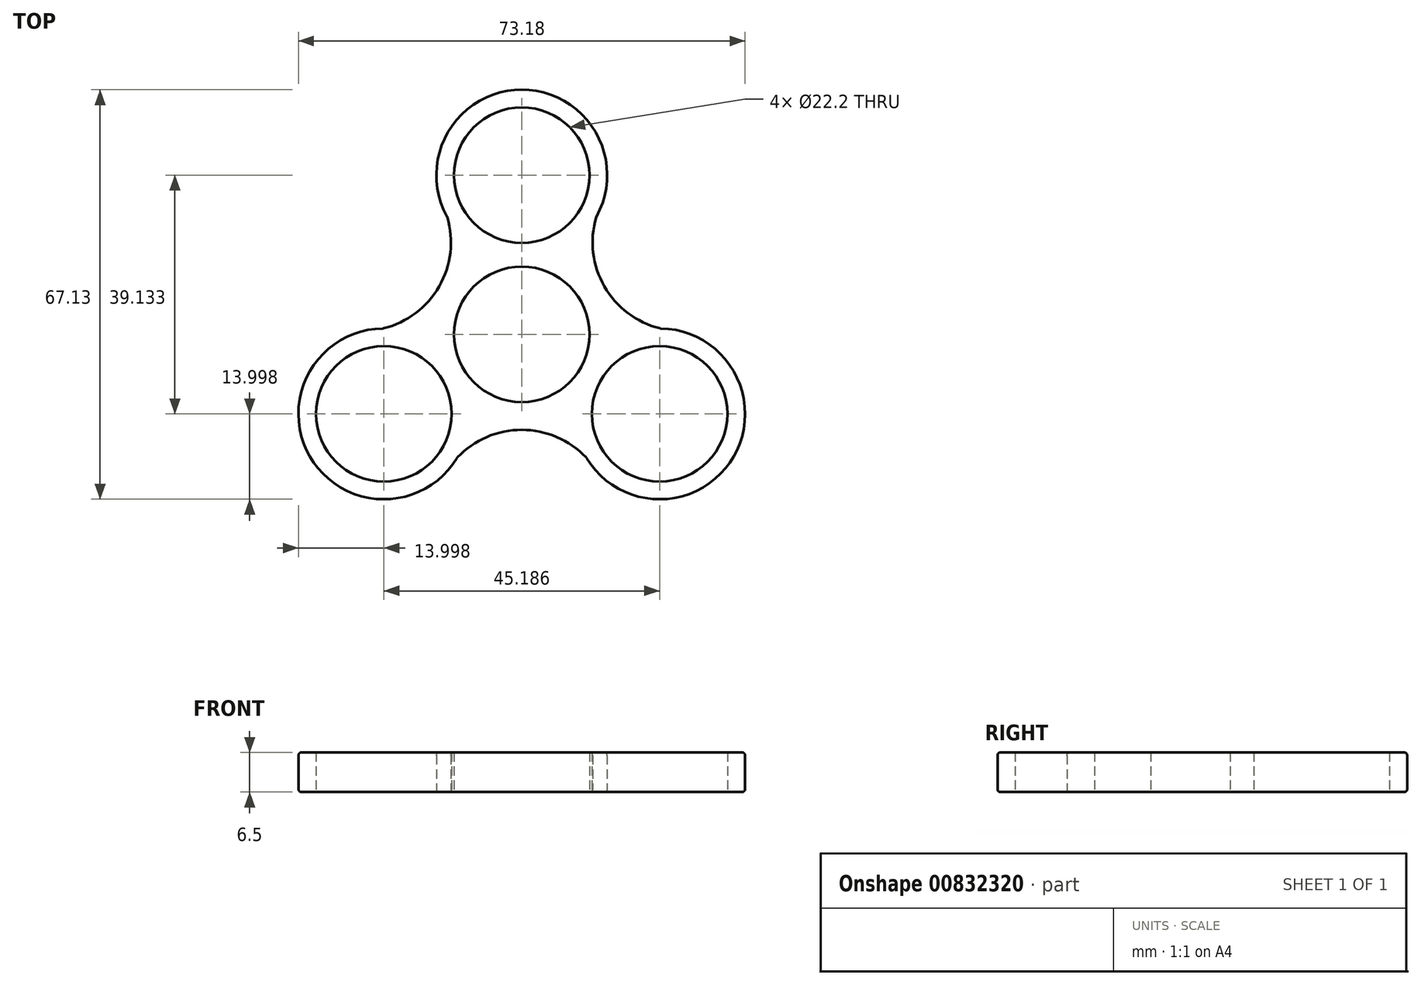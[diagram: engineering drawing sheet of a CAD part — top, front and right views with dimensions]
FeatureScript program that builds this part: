
annotation { "Feature Type Name" : "Feature", "Feature Type Description" : "" }
export const myFeature = defineFeature(function(context is Context, id is Id, definition is map)
    precondition{}
    {
        {
            var Q0;
            Q0=qCreatedBy(makeId("Top.planeOp"),FACE);
            var sketch = newSketch(context, id + "F0", { "sketchPlane" : qUnion([Q0])});
            skCircle(sketch, "E0", {"center": v(0, 0) * mm, "radius": 11.1 * mm});
            skCircle(sketch, "E1", {"center": v(0, 0) * mm, "radius": 14 * mm});
            skCircle(sketch, "E2", {"center": v(0, 26.1) * mm, "radius": 14 * mm});
            skCircle(sketch, "E3", {"center": v(0, 26.1) * mm, "radius": 11.1 * mm});
            skCircle(sketch, "E4.1.0", {"center": v(-22.6, -13.03) * mm, "radius": 11.1 * mm});
            skCircle(sketch, "E4.1.1", {"center": v(-22.6, -13.03) * mm, "radius": 14 * mm});
            skCircle(sketch, "E4.2.0", {"center": v(22.6, -13.03) * mm, "radius": 11.1 * mm});
            skCircle(sketch, "E4.2.1", {"center": v(22.6, -13.03) * mm, "radius": 14 * mm});
            skPoint(sketch, "E4.center", {"position": v(0, 0.01) * mm});
            skArc(sketch, "E5", {"start": v(12.47, -22.7) * mm, "mid": v(0, -15.65) * mm, "end": v(-12.47, -22.7) * mm});
            skArc(sketch, "E6.1.0", {"start": v(13.43, 22.15) * mm, "mid": v(13.55, 7.83) * mm, "end": v(25.9, 0.55) * mm});
            skArc(sketch, "E6.2.0", {"start": v(-25.9, 0.55) * mm, "mid": v(-13.56, 7.82) * mm, "end": v(-13.43, 22.15) * mm});
            skSolve(sketch);
        }
        {
            var Q0;
            Q0 = qSketchRegion(id + "F0", true);
            var Q1;
            Q1=makeQuery(id+"F0.imprint","IMPRINT",FACE,{"disambiguationData":[TD([[makeQuery(id+"F0.imprint","IMPRINT",EDGE,{"derivedFrom":sQuery(id+"F0.wireOp",EDGE,"E0")}),-1.0]])]});
            var Q2;
            {var subQ0=sQuery(id+"F0.wireOp",EDGE,"E4.1.1");var subQ1=sQuery(id+"F0.wireOp",EDGE,"E1");var subQ2=makeQuery(id+"F0.imprint","INTERSECT",VERTEX,{"disambiguationData":[OD(0.0)],"derivedFrom":[subQ1,subQ0]});Q2=makeQuery(id+"F0.imprint","IMPRINT",FACE,{"disambiguationData":[TD([[makeQuery(id+"F0.imprint","IMPRINT",EDGE,{"disambiguationData":[TD([[subQ2,-1.0]])],"derivedFrom":subQ1}),1.0]])]});}
            var Q3;
            {var subQ0=sQuery(id+"F0.wireOp",EDGE,"E4.2.1");var subQ1=sQuery(id+"F0.wireOp",EDGE,"E1");var subQ2=makeQuery(id+"F0.imprint","INTERSECT",VERTEX,{"disambiguationData":[OD(0.0)],"derivedFrom":[subQ1,subQ0]});Q3=makeQuery(id+"F0.imprint","IMPRINT",FACE,{"disambiguationData":[TD([[makeQuery(id+"F0.imprint","IMPRINT",EDGE,{"disambiguationData":[TD([[subQ2,-1.0]])],"derivedFrom":subQ1}),1.0]])]});}
            var Q4;
            {var subQ0=sQuery(id+"F0.wireOp",EDGE,"E2");var subQ1=sQuery(id+"F0.wireOp",EDGE,"E1");var subQ2=makeQuery(id+"F0.imprint","INTERSECT",VERTEX,{"disambiguationData":[OD(0.0)],"derivedFrom":[subQ1,subQ0]});Q4=makeQuery(id+"F0.imprint","IMPRINT",FACE,{"disambiguationData":[TD([[makeQuery(id+"F0.imprint","IMPRINT",EDGE,{"disambiguationData":[TD([[subQ2,1.0]])],"derivedFrom":subQ1}),1.0]])]});}
            extrude(context, id + "F1", {"entities" : qUnion([Q0, Q1, Q2, Q3, Q4]), "depth" : 6.5 * mm, "offsetDistance" : 25 * mm});
        }
        {
            var Q0;
            Q0=makeQuery(id+"F1.opExtrude","SWEPT_FACE",FACE,{"disambiguationData":[OSD([sQuery(id+"F0.wireOp",EDGE,"E4.1.1")])]});
            var Q1;
            Q1=makeQuery(id+"F1.opExtrude","SWEPT_FACE",FACE,{"disambiguationData":[OSD([sQuery(id+"F0.wireOp",EDGE,"E6.2.0")])]});
            var Q2;
            Q2=makeQuery(id+"F1.opExtrude","SWEPT_FACE",FACE,{"disambiguationData":[OSD([sQuery(id+"F0.wireOp",EDGE,"E2")])]});
            var Q3;
            Q3=makeQuery(id+"F1.opExtrude","SWEPT_FACE",FACE,{"disambiguationData":[OSD([sQuery(id+"F0.wireOp",EDGE,"E6.1.0")])]});
            var Q4;
            Q4=makeQuery(id+"F1.opExtrude","SWEPT_FACE",FACE,{"disambiguationData":[OSD([sQuery(id+"F0.wireOp",EDGE,"E4.2.1")])]});
            var Q5;
            Q5=makeQuery(id+"F1.opExtrude","SWEPT_FACE",FACE,{"disambiguationData":[OSD([sQuery(id+"F0.wireOp",EDGE,"E5")])]});
            fillet(context, id + "F2", {"entities" : qUnion([Q0, Q1, Q2, Q3, Q4, Q5]), "radius" : 0.5 * mm, "tangentPropagation" : true, "allowEdgeOverflow" : false});
        }
    });
